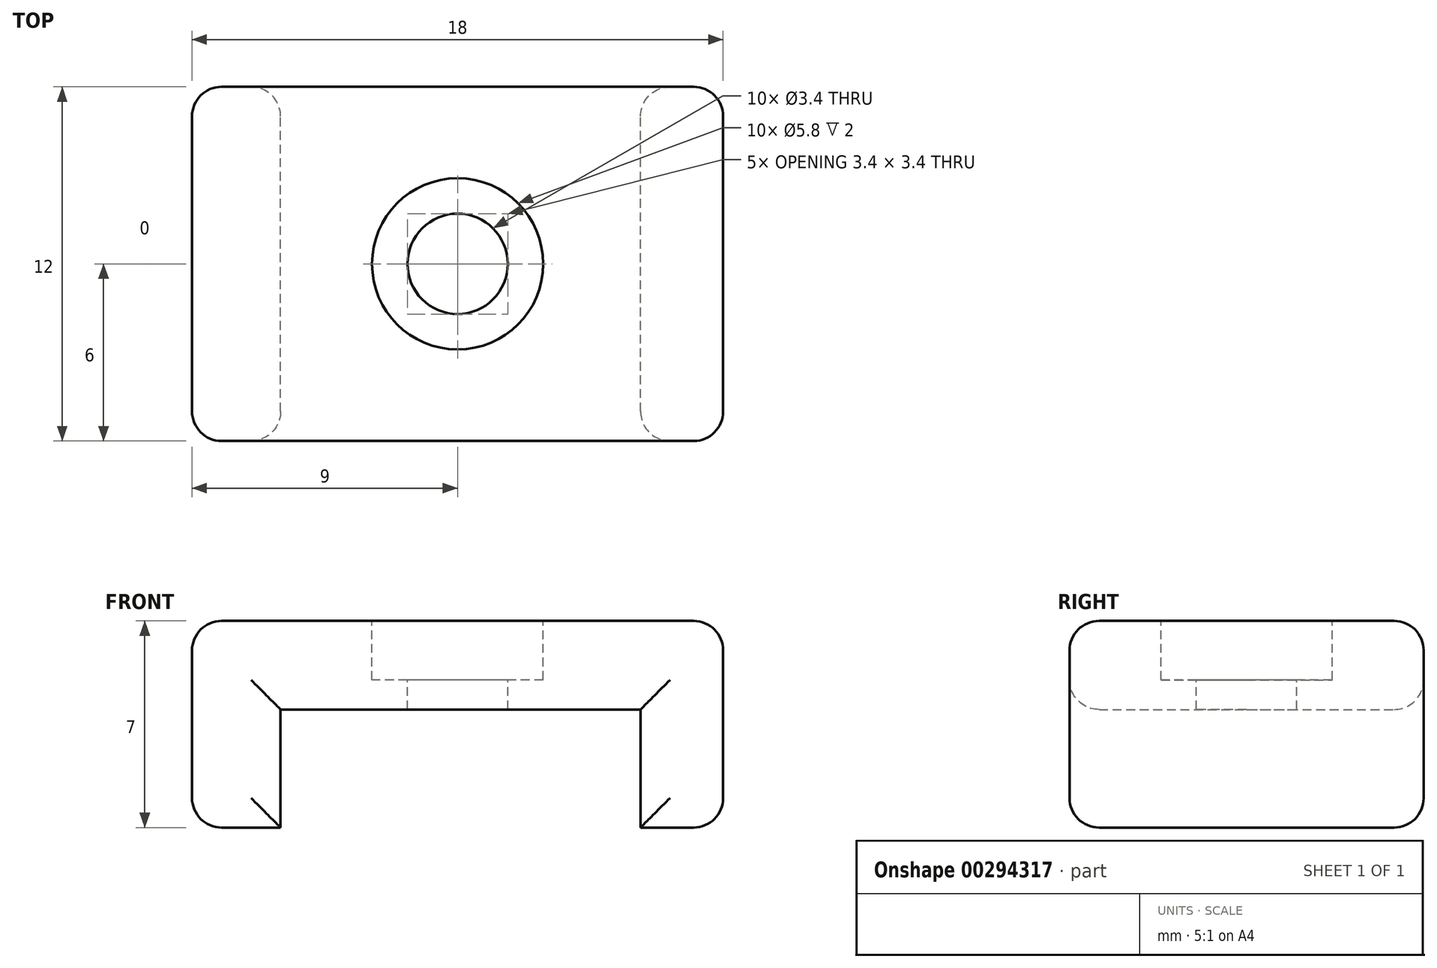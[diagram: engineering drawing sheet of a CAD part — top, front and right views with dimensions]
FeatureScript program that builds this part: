
annotation { "Feature Type Name" : "Feature", "Feature Type Description" : "" }
export const myFeature = defineFeature(function(context is Context, id is Id, definition is map)
    precondition{}
    {
        {
            var Q0;
            Q0=qCreatedBy(makeId("Front.planeOp"),FACE);
            var sketch = newSketch(context, id + "F0", { "sketchPlane" : qUnion([Q0])});
            skLineSegment(sketch, "E0.bottom", {"start": v(9, 3.5) * mm, "end": v(-9, 3.5) * mm});
            skLineSegment(sketch, "E0.top", {"start": v(9, -3.5) * mm, "end": v(6.2, -3.5) * mm});
            skLineSegment(sketch, "E0.left", {"start": v(9, 3.5) * mm, "end": v(9, -3.5) * mm});
            skLineSegment(sketch, "E0.right", {"start": v(-9, 3.5) * mm, "end": v(-9, -3.5) * mm});
            skPoint(sketch, "E0.middle", {"position": v(0, 0) * mm});
            skLineSegment(sketch, "E1.bottom", {"start": v(6.2, 0.5) * mm, "end": v(-6, 0.5) * mm});
            skLineSegment(sketch, "E1.left", {"start": v(6.2, 0.5) * mm, "end": v(6.2, -3.5) * mm});
            skLineSegment(sketch, "E1.right", {"start": v(-6, 0.5) * mm, "end": v(-6, -3.5) * mm});
            skLineSegment(sketch, "E2.trimOffspring", {"start": v(-6, -3.5) * mm, "end": v(-9, -3.5) * mm});
            skSolve(sketch);
        }
        {
            var Q0;
            Q0 = qSketchRegion(id + "F0", true);
            extrude(context, id + "F1", {"entities" : qUnion([Q0]), "depth" : 12 * mm});
        }
        {
            var Q0;
            Q0=makeQuery(id+"F1.opExtrude","SWEPT_FACE",FACE,{"disambiguationData":[OSD([sQuery(id+"F0.wireOp",EDGE,"E0.bottom")])]});
            var sketch = newSketch(context, id + "F2", { "sketchPlane" : qUnion([Q0])});
            skLineSegment(sketch, "E3", {"start": v(-9, 0) * mm, "end": v(9, -12) * mm, "construction": true});
            skCircle(sketch, "E4", {"center": v(0, -6) * mm, "radius": 2.9 * mm});
            skCircle(sketch, "E5", {"center": v(0, -6) * mm, "radius": 1.7 * mm});
            skSolve(sketch);
        }
        {
            var Q0;
            Q0=makeQuery(id+"F2.imprint","IMPRINT",FACE,{"disambiguationData":[TD([[makeQuery(id+"F2.imprint","IMPRINT",EDGE,{"derivedFrom":sQuery(id+"F2.wireOp",EDGE,"E5")}),1.0]])]});
            extrude(context, id + "F3", {"entities" : qUnion([Q0]), "operationType" : NewBodyOperationType.REMOVE, "endBound" : BoundingType.THROUGH_ALL, "oppositeDirection" : true, "depth" : 3 * mm});
        }
        {
            var Q0;
            Q0 = qSketchRegion(id + "F2", true);
            extrude(context, id + "F4", {"entities" : qUnion([Q0]), "operationType" : NewBodyOperationType.REMOVE, "oppositeDirection" : true, "depth" : 2 * mm});
        }
        {
            var Q0;
            Q0=makeQuery(id+"F1.opExtrude","CAP_FACE",FACE,{"disambiguationData":[OSD([sQuery(id+"F0.wireOp",EDGE,"E0.bottom"),sQuery(id+"F0.wireOp",EDGE,"E0.top"),sQuery(id+"F0.wireOp",EDGE,"E0.left"),sQuery(id+"F0.wireOp",EDGE,"E0.right"),sQuery(id+"F0.wireOp",EDGE,"E1.bottom"),sQuery(id+"F0.wireOp",EDGE,"E1.left"),sQuery(id+"F0.wireOp",EDGE,"E1.right"),sQuery(id+"F0.wireOp",EDGE,"E2.trimOffspring")])],"isStart":false});
            var Q1;
            Q1=makeQuery(id+"F1.opExtrude","CAP_FACE",FACE,{"disambiguationData":[OSD([sQuery(id+"F0.wireOp",EDGE,"E0.bottom"),sQuery(id+"F0.wireOp",EDGE,"E0.top"),sQuery(id+"F0.wireOp",EDGE,"E0.left"),sQuery(id+"F0.wireOp",EDGE,"E0.right"),sQuery(id+"F0.wireOp",EDGE,"E1.bottom"),sQuery(id+"F0.wireOp",EDGE,"E1.left"),sQuery(id+"F0.wireOp",EDGE,"E1.right"),sQuery(id+"F0.wireOp",EDGE,"E2.trimOffspring")])],"isStart":true});
            var Q2;
            Q2=makeQuery(id+"F1.opExtrude","SWEPT_EDGE",EDGE,{"disambiguationData":[OSD([sQuery(id+"F0.wireOp",EDGE,"E0.top"),sQuery(id+"F0.wireOp",EDGE,"E0.left")])]});
            var Q3;
            Q3=makeQuery(id+"F1.opExtrude","SWEPT_EDGE",EDGE,{"disambiguationData":[OSD([sQuery(id+"F0.wireOp",EDGE,"E0.right"),sQuery(id+"F0.wireOp",EDGE,"E2.trimOffspring")])]});
            var Q4;
            Q4=makeQuery(id+"F1.opExtrude","SWEPT_EDGE",EDGE,{"disambiguationData":[OSD([sQuery(id+"F0.wireOp",EDGE,"E0.bottom"),sQuery(id+"F0.wireOp",EDGE,"E0.right")])]});
            var Q5;
            Q5=makeQuery(id+"F1.opExtrude","SWEPT_EDGE",EDGE,{"disambiguationData":[OSD([sQuery(id+"F0.wireOp",EDGE,"E0.bottom"),sQuery(id+"F0.wireOp",EDGE,"E0.left")])]});
            fillet(context, id + "F5", {"entities" : qUnion([Q0, Q1, Q2, Q3, Q4, Q5]), "radius" : 1 * mm, "tangentPropagation" : true, "allowEdgeOverflow" : false});
        }
    });
